FCSTD DOCUMENT  (FreeCAD 1.0R39319 (Git))
Label: 30M_LysTaarn
License: All rights reserved
LicenseURL: http://en.wikipedia.org/wiki/All_rights_reserved
objects: Sketcher::SketchObject×3, PartDesign::Body×2, Image::ImagePlane×1, App::VarSet×1, PartDesign::SubShapeBinder×1
note: 9 computed .brp shape members not serialized (recipe doc carries the construction recipe); baked Part::Feature solids carry a one-line shape summary decoded from their .brp

FEATURE [Image::ImagePlane] Taarn
  Placement = pos=(-63.6,157.127,0) rot=(0,0,1;0.013963rad)
  XSize = 407.333
  YSize = 576.179
FEATURE [App::VarSet] VarSet
  IronAngle = 0
  IronWidth = 1.5
  LadderSection1Height = 0
  LadderSection2Height = 0
  LadderSection3Height = 0
  LadderStepHeight = 0
  LadderWidth = 0
  TowerHeigth = 664
  TowerSection1BottomWidth = 47
  TowerSection1Height = 220
  TowerSection1TopWidth = 26
  TowerSection2BottomWidth = 0
  TowerSection2Height = 0
  TowerSection2TopWidth = 0
  TowerSection3BottomWidth = 0
  TowerSection3Height = 0
  TowerSection3TopWidth = 0
  expr: TowerHeigth = 355 + 309
FEATURE [Sketcher::SketchObject] Sketch  label="Measurements"
  ArcFitTolerance = 1e-06
  AttachmentSupport = -> [XY_Plane]
  FullyConstrained = false
  MakeInternals = false
  MapMode = 5
  expr: Constraints[1] = VarSet.TowerSection1BottomWidth
  sketch-geometry (14):
    g0: LineSegment StartX=-23.5 StartY=0 StartZ=0 EndX=23.5 EndY=0 EndZ=0
    g1: LineSegment StartX=-85.2951 StartY=302.62 StartZ=0 EndX=-59.2897 EndY=302.62 EndZ=0
    g2: LineSegment StartX=0 StartY=0 StartZ=0 EndX=0 EndY=354.583 EndZ=0
    g3: LineSegment StartX=-72.2924 StartY=-2.05836 StartZ=0 EndX=-72.2924 EndY=302.62 EndZ=0
    g4: LineSegment StartX=-103.565 StartY=268.57 StartZ=0 EndX=-92.7344 EndY=268.57 EndZ=0
    g5: GeomPoint X=0.347345 Y=221.58 Z=0
    g6: GeomPoint X=-145.856 Y=302.828 Z=0
    g7: GeomPoint X=-143.509 Y=81.3065 Z=0
    g8: GeomPoint X=17.5859 Y=240.545 Z=0
    g9: GeomPoint X=-12.1586 Y=0 Z=0
    g10: GeomPoint X=-76.9798 Y=163.023 Z=0
    g11: GeomPoint X=-67.324 Y=163.023 Z=0
    g12: GeomPoint X=-67.0278 Y=156.448 Z=0
    g13: GeomPoint X=-20.204 Y=0 Z=0
  constraints (20):
    c: Horizontal(g0)
    c: DistanceX(g0,g0) = 47
    c: Symmetric(g0,g0,g-1)
    c: Horizontal(g1)
    c: DistanceX(g1,g1) = 26.0054
    c: Coincident(g2,g-1)
    c: PointOnObject(g2,g-2)
    c: DistanceY(g2,g2) = 354.583
    c: Symmetric(g1,g1,g3)
    c: Vertical(g3)
    c: DistanceY(g3,g3) = 304.679
    c: Horizontal(g4)
    c: Distance(g4,g4) = 10.8308
    c: DistanceY(g2,g5) = 221.58
    c: DistanceY(g7,g6) = 221.522
    c: PointOnObject(g9,g0)
    c: Distance(g8,g9) = 242.377
    c: DistanceY(g12,g11) = 6.57539
    c: DistanceX(g10,g11) = 9.65575
    c: PointOnObject(g13,g0)
FEATURE [Sketcher::SketchObject] Sketch001  label="BasicGitterSketch"
  ArcFitTolerance = 1e-06
  AttachmentSupport = -> [XY_Plane]
  FullyConstrained = false
  MakeInternals = false
  MapMode = 5
  expr: Constraints[115] = VarSet.IronWidth
  expr: Constraints[7] = VarSet.TowerSection1BottomWidth
  expr: Constraints[8] = VarSet.TowerSection1TopWidth
  expr: Constraints[9] = VarSet.TowerHeigth
  sketch-geometry (56):
    g0: LineSegment StartX=-13 StartY=664 StartZ=0 EndX=-23.5 EndY=0 EndZ=0
    g1: LineSegment StartX=-23.5 StartY=0 StartZ=0 EndX=23.5 EndY=0 EndZ=0
    g2: LineSegment StartX=23.5 StartY=0 StartZ=0 EndX=13 EndY=664 EndZ=0
    g3: LineSegment StartX=13 StartY=664 StartZ=0 EndX=-13 EndY=664 EndZ=0
    g4: LineSegment StartX=-23.4763 StartY=1.5 StartZ=0 EndX=23.0986 EndY=25.3867 EndZ=0
    g5: LineSegment StartX=23.0986 StartY=25.3867 StartZ=0 EndX=-22.7269 EndY=48.8891 EndZ=0
    g6: LineSegment [constr] StartX=-23.4763 StartY=1.5 StartZ=0 EndX=23.4763 EndY=1.5 EndZ=0
    g7: ArcOfCircle [constr] CenterX=-23.4763 CenterY=1.5 CenterZ=0 NormalX=0 NormalY=0 NormalZ=1 AngleXU=0 Radius=26.1715 StartAngle=0 EndAngle=0.473889
    g8: ArcOfCircle [constr] CenterX=23.0986 CenterY=25.3867 CenterZ=0 NormalX=0 NormalY=0 NormalZ=1 AngleXU=0 Radius=26.1715 StartAngle=2.6677 EndAngle=3.61548
    g9: LineSegment [constr] StartX=-3.07295 StartY=25.3867 StartZ=0 EndX=23.0986 EndY=25.3867 EndZ=0
    g10: LineSegment [constr] StartX=-0.188863 StartY=37.3301 StartZ=0 EndX=-0.188863 EndY=25.3867 EndZ=0
    g11: LineSegment [constr] StartX=-0.188863 StartY=13.4434 StartZ=0 EndX=-0.188863 EndY=25.3867 EndZ=0
    g12: LineSegment [constr] StartX=-0.188863 StartY=13.4434 StartZ=0 EndX=-0.188863 EndY=1.5 EndZ=0
    g13: LineSegment [constr] StartX=-112.334 StartY=1.5 StartZ=0 EndX=-112.334 EndY=0 EndZ=0
    g14: LineSegment StartX=-22.7269 StartY=48.8891 StartZ=0 EndX=22.3612 EndY=72.0134 EndZ=0
    g15: LineSegment StartX=22.3612 StartY=72.0134 StartZ=0 EndX=-22.0014 EndY=94.7656 EndZ=0
    g16: LineSegment StartX=-22.0014 StartY=94.7656 StartZ=0 EndX=21.6475 EndY=117.152 EndZ=0
    g17: LineSegment StartX=21.6475 StartY=117.152 StartZ=0 EndX=-21.2991 EndY=139.178 EndZ=0
    g18: LineSegment StartX=-21.2991 StartY=139.178 StartZ=0 EndX=20.9565 EndY=160.849 EndZ=0
    g19: LineSegment StartX=20.9565 StartY=160.849 StartZ=0 EndX=-20.6193 EndY=182.172 EndZ=0
    g20: LineSegment StartX=-20.6193 StartY=182.172 StartZ=0 EndX=20.2875 EndY=203.152 EndZ=0
    g21: LineSegment StartX=20.2875 StartY=203.152 StartZ=0 EndX=-19.9611 EndY=223.794 EndZ=0
    g22: LineSegment StartX=-19.9374 StartY=225.294 StartZ=0 EndX=19.9374 EndY=225.294 EndZ=0
    g23: LineSegment [constr] StartX=-112.334 StartY=225.294 StartZ=0 EndX=-112.334 EndY=223.794 EndZ=0
    g24: LineSegment [constr] StartX=-112.334 StartY=225.294 StartZ=0 EndX=-112.334 EndY=226.794 EndZ=0
    g25: LineSegment StartX=-19.9137 StartY=226.794 StartZ=0 EndX=19.5932 EndY=247.056 EndZ=0
    g26: LineSegment StartX=19.5932 StartY=247.056 StartZ=0 EndX=-19.278 EndY=266.992 EndZ=0
    g27: LineSegment StartX=-19.278 StartY=266.992 StartZ=0 EndX=18.9678 EndY=286.607 EndZ=0
    g28: LineSegment StartX=18.9678 StartY=286.607 StartZ=0 EndX=-18.6626 EndY=305.906 EndZ=0
    g29: LineSegment StartX=-18.6626 StartY=305.906 StartZ=0 EndX=18.3624 EndY=324.895 EndZ=0
    g30: LineSegment StartX=18.3624 StartY=324.895 StartZ=0 EndX=-18.0669 EndY=343.578 EndZ=0
    g31: LineSegment StartX=-18.0669 StartY=343.578 StartZ=0 EndX=17.7762 EndY=361.961 EndZ=0
    g32: LineSegment StartX=17.7762 StartY=361.961 StartZ=0 EndX=-17.4902 EndY=380.048 EndZ=0
    g33: LineSegment StartX=-17.4902 StartY=380.048 StartZ=0 EndX=17.2088 EndY=397.844 EndZ=0
    g34: LineSegment StartX=17.2088 StartY=397.844 StartZ=0 EndX=-16.9319 EndY=415.354 EndZ=0
    g35: LineSegment StartX=-16.9319 StartY=415.354 StartZ=0 EndX=17.2088 EndY=397.844 EndZ=0
    g36: LineSegment StartX=-16.9319 StartY=415.354 StartZ=0 EndX=16.6595 EndY=432.582 EndZ=0
    g37: LineSegment StartX=16.6595 StartY=432.582 StartZ=0 EndX=-16.3914 EndY=449.532 EndZ=0
    g38: LineSegment [constr] StartX=-112.334 StartY=451.032 StartZ=0 EndX=-112.334 EndY=449.532 EndZ=0
    g39: LineSegment StartX=-16.3677 StartY=451.032 StartZ=0 EndX=16.3677 EndY=451.032 EndZ=0
    g40: LineSegment [constr] StartX=-112.334 StartY=451.032 StartZ=0 EndX=-112.334 EndY=452.532 EndZ=0
    g41: LineSegment StartX=-16.344 StartY=452.532 StartZ=0 EndX=16.081 EndY=469.162 EndZ=0
    g42: LineSegment StartX=16.081 StartY=469.162 StartZ=0 EndX=-15.8223 EndY=485.524 EndZ=0
    g43: LineSegment StartX=-15.8223 StartY=485.524 StartZ=0 EndX=15.5677 EndY=501.623 EndZ=0
    g44: LineSegment StartX=15.5677 StartY=501.623 StartZ=0 EndX=-15.3172 EndY=517.463 EndZ=0
    g45: LineSegment StartX=-15.3172 StartY=517.463 StartZ=0 EndX=15.0708 EndY=533.048 EndZ=0
    g46: LineSegment StartX=15.0708 StartY=533.048 StartZ=0 EndX=-14.8283 EndY=548.382 EndZ=0
    g47: LineSegment StartX=-14.8283 StartY=548.382 StartZ=0 EndX=14.5897 EndY=563.47 EndZ=0
    g48: LineSegment StartX=14.5897 StartY=563.47 StartZ=0 EndX=-14.355 EndY=578.315 EndZ=0
    g49: LineSegment StartX=-14.355 StartY=578.315 StartZ=0 EndX=14.124 EndY=592.921 EndZ=0
    g50: LineSegment StartX=14.124 StartY=592.921 StartZ=0 EndX=-13.8967 EndY=607.292 EndZ=0
    g51: LineSegment StartX=-13.8967 StartY=607.292 StartZ=0 EndX=13.6731 EndY=621.431 EndZ=0
    g52: LineSegment StartX=13.6731 StartY=621.431 StartZ=0 EndX=-13.4532 EndY=635.344 EndZ=0
    g53: LineSegment StartX=-13.4532 StartY=635.344 StartZ=0 EndX=13.2367 EndY=649.032 EndZ=0
    g54: LineSegment StartX=13.2367 StartY=649.032 StartZ=0 EndX=-13.0237 EndY=662.5 EndZ=0
    g55: LineSegment [constr] StartX=-112.334 StartY=664 StartZ=0 EndX=-112.334 EndY=662.5 EndZ=0
  constraints (178):
    c: Coincident(g0,g1)
    c: Horizontal(g1)
    c: Coincident(g1,g2)
    c: Coincident(g2,g3)
    c: Coincident(g3,g0)
    c: Symmetric(g2,g0,g-2)
    c: Symmetric(g1,g0,g-1)
    c: DistanceX(g0,g1) = 47
    c: Distance(g3,g3) = 26
    c: DistanceY(g1,g2) = 664
    c: PointOnObject(g4,g0)
    c: PointOnObject(g4,g2)
    c: Coincident(g4,g5)
    c: PointOnObject(g5,g0)
    c: Coincident(g4,g6)
    c: PointOnObject(g6,g2)
    c: Horizontal(g6)
    c: Coincident(g7,g4)
    c: PointOnObject(g7,g4)
    c: PointOnObject(g7,g6)
    c: Coincident(g8,g4)
    c: PointOnObject(g8,g5)
    c: Equal(g7,g8)
    c: PointOnObject(g9,g8)
    c: Coincident(g9,g4)
    c: Horizontal(g9)
    c: Coincident(g10,g8)
    c: PointOnObject(g10,g9)
    c: Coincident(g11,g8)
    c: Coincident(g11,g10)
    c: Vertical(g11)
    c: Vertical(g10)
    c: Coincident(g12,g7)
    c: PointOnObject(g12,g6)
    c: Vertical(g12)
    c: Coincident(g8,g7)
    c: PointOnObject(g13,g-1)
    c: Vertical(g13)
    c: Horizontal(g13,g4)
    c: Coincident(g5,g14)
    c: PointOnObject(g14,g2)
    c: Coincident(g14,g15)
    c: PointOnObject(g15,g0)
    c: Coincident(g15,g16)
    c: PointOnObject(g16,g2)
    c: Coincident(g16,g17)
    c: PointOnObject(g17,g0)
    c: Coincident(g17,g18)
    c: PointOnObject(g18,g2)
    c: Coincident(g18,g19)
    c: PointOnObject(g19,g0)
    c: Coincident(g19,g20)
    c: PointOnObject(g20,g2)
    c: Coincident(g20,g21)
    c: PointOnObject(g21,g0)
    c: Parallel(g4,g14)
    c: Parallel(g14,g16)
    c: Parallel(g16,g18)
    c: Parallel(g18,g20)
    c: Parallel(g5,g15)
    c: Parallel(g15,g17)
    c: Parallel(g17,g19)
    c: Parallel(g19,g21)
    c: PointOnObject(g22,g0)
    c: PointOnObject(g22,g2)
    c: Horizontal(g22)
    c: Vertical(g23)
    c: Horizontal(g23,g21)
    c: Horizontal(g22,g23)
    c: Equal(g23,g13)
    c: Coincident(g24,g23)
    c: Vertical(g24)
    c: Equal(g24,g23)
    c: PointOnObject(g25,g0)
    c: PointOnObject(g25,g2)
    c: Coincident(g25,g26)
    c: PointOnObject(g26,g0)
    c: Coincident(g26,g27)
    c: PointOnObject(g27,g2)
    c: Coincident(g27,g28)
    c: PointOnObject(g28,g0)
    c: Coincident(g28,g29)
    c: PointOnObject(g29,g2)
    c: Coincident(g29,g30)
    c: PointOnObject(g30,g0)
    c: Coincident(g30,g31)
    c: PointOnObject(g31,g2)
    c: Coincident(g31,g32)
    c: PointOnObject(g32,g0)
    c: Coincident(g32,g33)
    c: PointOnObject(g33,g2)
    c: Coincident(g33,g34)
    c: PointOnObject(g34,g0)
    c: Coincident(g34,g35)
    c: PointOnObject(g35,g2)
    c: Parallel(g21,g26)
    c: Parallel(g26,g28)
    c: Parallel(g28,g30)
    c: Parallel(g30,g32)
    c: Parallel(g32,g35)
    c: Parallel(g32,g34)
    c: Horizontal(g25,g24)
    c: Parallel(g25,g20)
    c: Parallel(g25,g27)
    c: Parallel(g29,g31)
    c: Parallel(g31,g33)
    c: Coincident(g34,g36)
    c: PointOnObject(g36,g2)
    c: Coincident(g36,g37)
    c: PointOnObject(g37,g0)
    c: Parallel(g33,g36)
    c: Parallel(g37,g34)
    c: Vertical(g38)
    c: Equal(g38,g24)
    c: Horizontal(g37,g38)
    c: DistanceY(g38,g38) = 1.5
    c: PointOnObject(g39,g0)
    c: PointOnObject(g39,g2)
    c: Horizontal(g39)
    c: Horizontal(g39,g38)
    c: Coincident(g40,g38)
    c: Equal(g40,g38)
    c: Vertical(g40)
    c: Coincident(g41,g42)
    c: Coincident(g42,g43)
    c: Coincident(g43,g44)
    c: Coincident(g44,g45)
    c: Coincident(g45,g46)
    c: Coincident(g46,g47)
    c: Coincident(g47,g48)
    c: Coincident(g48,g49)
    c: Coincident(g49,g50)
    c: Coincident(g50,g51)
    c: Coincident(g51,g52)
    c: Coincident(g52,g53)
    c: Coincident(g53,g54)
    c: Vertical(g55)
    c: Equal(g55,g40)
    c: PointOnObject(g54,g0)
    c: PointOnObject(g52,g0)
    c: PointOnObject(g50,g0)
    c: PointOnObject(g48,g0)
    c: PointOnObject(g46,g0)
    c: PointOnObject(g44,g0)
    c: PointOnObject(g42,g0)
    c: PointOnObject(g41,g0)
    c: Parallel(g41,g43)
    c: Parallel(g41,g36)
    c: Parallel(g42,g37)
    c: Horizontal(g41,g40)
    c: Horizontal(g55,g54)
    c: Horizontal(g55,g0)
    c: PointOnObject(g53,g2)
    c: PointOnObject(g51,g2)
    c: PointOnObject(g49,g2)
    c: PointOnObject(g47,g2)
    c: PointOnObject(g45,g2)
    c: PointOnObject(g43,g2)
    c: Parallel(g44,g46)
    c: Parallel(g44,g42)
    c: PointOnObject(g41,g2)
    c: Parallel(g45,g43)
    c: Parallel(g47,g45)
    c: Parallel(g48,g46)
    c: Parallel(g49,g47)
    c: Parallel(g50,g48)
    c: Parallel(g51,g49)
    c: Parallel(g49,g53)
    c: Parallel(g52,g50)
    c: Parallel(g54,g52)
    c: Angle(g50,g51) = 0.947777
    c: Parallel(g29,g27)
    c: Vertical(g38,g24)
    c: Vertical(g23,g13)
    c: DistanceY(g22,g39) = 225.739
    c: DistanceY(g39,g2) = 212.968
    c: DistanceY(g-1,g22) = 225.294
    c: Vertical(g55,g40)
FEATURE [PartDesign::Body] Body  label="BasisBody"
  AllowCompound = true
  Group = -> [Sketch,Sketch001]
  Origin = -> Origin
FEATURE [PartDesign::SubShapeBinder] Binder
  BindCopyOnChange = 0
  BindMode = 0
  ClaimChildren = false
  Context = -> Body001 [Binder.]
  Fuse = false
  MakeFace = true
  OffsetFill = false
  OffsetIntersection = false
  OffsetJoinType = 0
  OffsetOpenResult = false
  PartialLoad = false
  Refine = true
  Relative = true
  Support = -> [Body[Sketch001.]]
  _Version = 2
FEATURE [Sketcher::SketchObject] Sketch002
  ArcFitTolerance = 1e-06
  AttachmentSupport = -> [XY_Plane001]
  ExternalGeometry = -> [Binder]
  FullyConstrained = true
  MakeInternals = false
  MapMode = 5
  expr: Constraints[28] = VarSet.IronWidth
  sketch-geometry (37):
    g0: LineSegment StartX=-18.0112 StartY=451.032 StartZ=0 EndX=-14.6435 EndY=664 EndZ=0
    g1: LineSegment StartX=-14.6435 StartY=664 StartZ=0 EndX=14.6435 EndY=664 EndZ=0
    g2: LineSegment StartX=14.6435 StartY=664 StartZ=0 EndX=18.0112 EndY=451.032 EndZ=0
    g3: LineSegment StartX=-11.4067 StartY=660.828 StartZ=0 EndX=-11.7828 EndY=637.043 EndZ=0
    g4: LineSegment StartX=-11.7828 StartY=637.043 StartZ=0 EndX=11.5932 EndY=649.032 EndZ=0
    g5: LineSegment StartX=11.5932 StartY=649.032 StartZ=0 EndX=-11.4067 EndY=660.828 EndZ=0
    g6: LineSegment StartX=-11.3802 StartY=662.5 StartZ=0 EndX=11.3802 EndY=662.5 EndZ=0
    g7: LineSegment StartX=11.3802 StartY=662.5 StartZ=0 EndX=11.5663 EndY=650.731 EndZ=0
    g8: LineSegment StartX=11.5663 StartY=650.731 StartZ=0 EndX=-11.3802 EndY=662.5 EndZ=0
    g9: LineSegment [constr] StartX=-14.6928 StartY=660.88 StartZ=0 EndX=-11.4067 EndY=660.828 EndZ=0
    g10: LineSegment [constr] StartX=11.3802 StartY=662.5 StartZ=0 EndX=14.6664 EndY=662.552 EndZ=0
    g11: LineSegment [constr] StartX=0.777791 StartY=656.265 StartZ=0 EndX=0.0932658 EndY=654.93 EndZ=0
    g12: LineSegment StartX=11.6197 StartY=647.36 StartZ=0 EndX=-11.8097 EndY=635.344 EndZ=0
    g13: LineSegment StartX=-11.8097 StartY=635.344 StartZ=0 EndX=12.0028 EndY=623.131 EndZ=0
    g14: LineSegment StartX=12.0028 StartY=623.131 StartZ=0 EndX=11.6197 EndY=647.36 EndZ=0
    g15: LineSegment StartX=-18.0112 StartY=451.032 StartZ=0 EndX=18.0112 EndY=451.032 EndZ=0
    g16: LineSegment StartX=-11.8361 StartY=633.671 StartZ=0 EndX=12.0297 EndY=621.431 EndZ=0
    g17: LineSegment StartX=12.0297 StartY=621.431 StartZ=0 EndX=-12.2264 EndY=608.991 EndZ=0
    g18: LineSegment StartX=-12.2264 StartY=608.991 StartZ=0 EndX=-11.8361 EndY=633.671 EndZ=0
    g19: LineSegment StartX=12.0561 StartY=619.759 StartZ=0 EndX=-12.2533 EndY=607.292 EndZ=0
    g20: LineSegment StartX=-12.2533 StartY=607.292 StartZ=0 EndX=12.4536 EndY=594.62 EndZ=0
    g21: LineSegment StartX=12.4536 StartY=594.62 StartZ=0 EndX=12.0561 EndY=619.759 EndZ=0
    g22: LineSegment StartX=-12.2797 StartY=605.619 StartZ=0 EndX=-12.6846 EndY=580.014 EndZ=0
    g23: LineSegment StartX=-12.6846 StartY=580.014 StartZ=0 EndX=12.4805 EndY=592.921 EndZ=0
    g24: LineSegment StartX=12.4805 StartY=592.921 StartZ=0 EndX=-12.2797 EndY=605.619 EndZ=0
    g25: LineSegment StartX=12.507 StartY=591.248 StartZ=0 EndX=-12.7115 EndY=578.315 EndZ=0
    g26: LineSegment StartX=-12.7115 StartY=578.315 StartZ=0 EndX=12.9194 EndY=565.17 EndZ=0
    g27: LineSegment StartX=12.9194 StartY=565.17 StartZ=0 EndX=12.507 EndY=591.248 EndZ=0
    g28: LineSegment StartX=-12.7379 StartY=576.643 StartZ=0 EndX=-13.1579 EndY=550.082 EndZ=0
    g29: LineSegment StartX=-13.1579 StartY=550.082 StartZ=0 EndX=12.9462 EndY=563.47 EndZ=0
    g30: LineSegment StartX=12.9462 StartY=563.47 StartZ=0 EndX=-12.7379 EndY=576.643 EndZ=0
    g31: LineSegment StartX=12.9727 StartY=561.798 StartZ=0 EndX=13.4004 EndY=534.748 EndZ=0
    g32: LineSegment StartX=13.4004 StartY=534.748 StartZ=0 EndX=-13.1848 EndY=548.382 EndZ=0
    g33: LineSegment StartX=-13.1848 StartY=548.382 StartZ=0 EndX=12.9727 EndY=561.798 EndZ=0
    g34: LineSegment StartX=14.464 StartY=467.49 StartZ=0 EndX=14.7005 EndY=452.532 EndZ=0
    g35: LineSegment StartX=14.464 StartY=467.49 StartZ=0 EndX=-14.7005 EndY=452.532 EndZ=0
    g36: LineSegment StartX=-14.7005 StartY=452.532 StartZ=0 EndX=14.7005 EndY=452.532 EndZ=0
  constraints (109):
    c: Coincident(g0,g1)
    c: Coincident(g1,g2)
    c: Parallel(g2,g-3)
    c: Parallel(g-4,g0)
    c: Symmetric(g0,g1,g-2)
    c: Coincident(g3,g4)
    c: Coincident(g4,g5)
    c: Coincident(g5,g3)
    c: Coincident(g6,g7)
    c: Coincident(g7,g8)
    c: Coincident(g8,g6)
    c: Parallel(g7,g-3)
    c: Parallel(g6,g-8)
    c: Parallel(g8,g-5)
    c: Parallel(g5,g-5)
    c: Parallel(g3,g-4)
    c: Parallel(g4,g-6)
    c: Coincident(g9,g3)
    c: PointOnObject(g9,g0)
    c: Symmetric(g9,g3,g-4)
    c: PointOnObject(g6,g3)
    c: Horizontal(g6,g-5)
    c: PointOnObject(g4,g7)
    c: Horizontal(g4,g-6)
    c: Coincident(g10,g6)
    c: PointOnObject(g10,g2)
    c: Symmetric(g6,g10,g-3)
    c: Symmetric(g11,g11,g-5)
    c: Distance(g11,g11) = 1.5
    c: Symmetric(g3,g4,g11)
    c: Horizontal(g0,g2)
    c: Distance(g9) = 3.28654
    c: Coincident(g12,g13)
    c: Coincident(g13,g14)
    c: Coincident(g14,g12)
    c: Horizontal(g12,g-7)
    c: PointOnObject(g12,g3)
    c: PointOnObject(g12,g7)
    c: PointOnObject(g13,g7)
    c: Parallel(g12,g-6)
    c: Parallel(g13,g-7)
    c: Horizontal(g1,g-8)
    c: Coincident(g15,g0)
    c: Coincident(g15,g2)
    c: Coincident(g16,g17)
    c: Coincident(g17,g18)
    c: Coincident(g18,g16)
    c: Coincident(g19,g20)
    c: Coincident(g20,g21)
    c: Coincident(g21,g19)
    c: Coincident(g22,g23)
    c: Coincident(g23,g24)
    c: Coincident(g24,g22)
    c: Parallel(g24,g20)
    c: Parallel(g20,g-19)
    c: Parallel(g19,g17)
    c: Parallel(g17,g-20)
    c: Parallel(g16,g-7)
    c: PointOnObject(g16,g3)
    c: PointOnObject(g17,g3)
    c: PointOnObject(g22,g18)
    c: PointOnObject(g22,g18)
    c: PointOnObject(g19,g18)
    c: Horizontal(g19,g-20)
    c: Horizontal(g16,g-20)
    c: PointOnObject(g16,g14)
    c: PointOnObject(g19,g14)
    c: PointOnObject(g20,g14)
    c: PointOnObject(g23,g21)
    c: Horizontal(g23,g-19)
    c: Parallel(g23,g-18)
    c: Coincident(g25,g26)
    c: Coincident(g26,g27)
    c: Coincident(g27,g25)
    c: Coincident(g28,g29)
    c: Coincident(g29,g30)
    c: Coincident(g30,g28)
    c: Coincident(g31,g32)
    c: Coincident(g32,g33)
    c: Coincident(g33,g31)
    c: Horizontal(g25,g-18)
    c: Horizontal(g29,g-17)
    c: Horizontal(g32,g-16)
    c: PointOnObject(g25,g21)
    c: PointOnObject(g26,g21)
    c: PointOnObject(g31,g27)
    c: PointOnObject(g31,g27)
    c: PointOnObject(g29,g27)
    c: PointOnObject(g28,g22)
    c: PointOnObject(g25,g22)
    c: PointOnObject(g28,g22)
    c: PointOnObject(g32,g28)
    c: Parallel(g32,g-15)
    c: Parallel(g33,g-16)
    c: Parallel(g-16,g29)
    c: Parallel(g30,g-17)
    c: Parallel(g-17,g26)
    c: Parallel(g-18,g25)
    c: Coincident(g34,g35)
    c: Coincident(g35,g36)
    c: Coincident(g36,g34)
    c: Parallel(g35,g-10)
    c: Parallel(g34,g-3)
    c: Parallel(g36,g-9)
    c: PointOnObject(g34,g31)
    c: Horizontal(g35,g-10)
    c: PointOnObject(g35,g28)
    c: PointOnObject(g2,g-9)
    c: Distance(g15,g15) = 36.0224
FEATURE [PartDesign::Body] Body001  label="MastTopSection"
  AllowCompound = true
  Group = -> [Binder,Sketch002]
  Origin = -> Origin001
